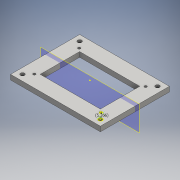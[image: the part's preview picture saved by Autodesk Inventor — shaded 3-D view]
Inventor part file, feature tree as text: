
AUTODESK INVENTOR PART (.ipt)
format: ipt  version: 2016 SP2 (Build 200236200, 236)  size: 151,040 bytes
history: native  units: mm
features: extrude x4, sketch x4, other x1, plane x1
ambient origin geometry x8: Origin, YZ Plane, XZ Plane, XY Plane, X Axis, Y Axis, Z Axis, Center Point
bodies: Solid1 (feature_tree)
feature tree (10):
  extrude  "Rim"  Depth=40.0mm
  extrude  "Pegs"  Depth=15.0mm
  extrude  "Bolt Holes"  Depth=5.0mm
  other  "For Construction"
  plane  "Work Plane2"
  extrude  "Bolt heads"  Depth=3.0mm
  sketch  "Sketch1"  dims[d0=61.0mm d1=40.0mm]
  sketch  "Sketch2"  dims[d2=15.0mm d3=15.0mm]
  sketch  "Sketch4"  dims[d4=5.0mm d5=0.0mm d6=67.4mm]
  sketch  "Sketch13"  dims[d7=45.53mm d8=2.5mm d9=3.0mm d10=0.0mm d17=3.0mm d18=0.0mm d19=5.265587mm d42=6.0mm d43=3.0mm d44=0.0mm]
